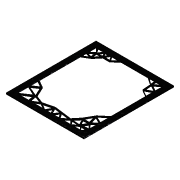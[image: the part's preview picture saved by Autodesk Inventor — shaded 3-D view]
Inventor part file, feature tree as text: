
AUTODESK INVENTOR PART (.ipt)
format: ipt  version: 2014 (Build 180170000, 170)  size: 233,472 bytes
history: native  units: mm
features: extrude x2, sketch x2
ambient origin geometry x8: Origin, YZ Plane, XZ Plane, XY Plane, X Axis, Y Axis, Z Axis, Center Point
bodies: Solid1 (feature_tree)
feature tree (4):
  extrude  "Extrusion1"  Depth=260.0mm
  extrude  "Extrusion2"  Depth=15.0mm
  sketch  "Sketch1"  dims[d0=225.0mm d1=260.0mm]
  sketch  "Sketch2"  dims[d2=4.0mm d3=0.0mm d4=15.0mm d5=15.0mm d6=4.0mm d7=0.0mm]
